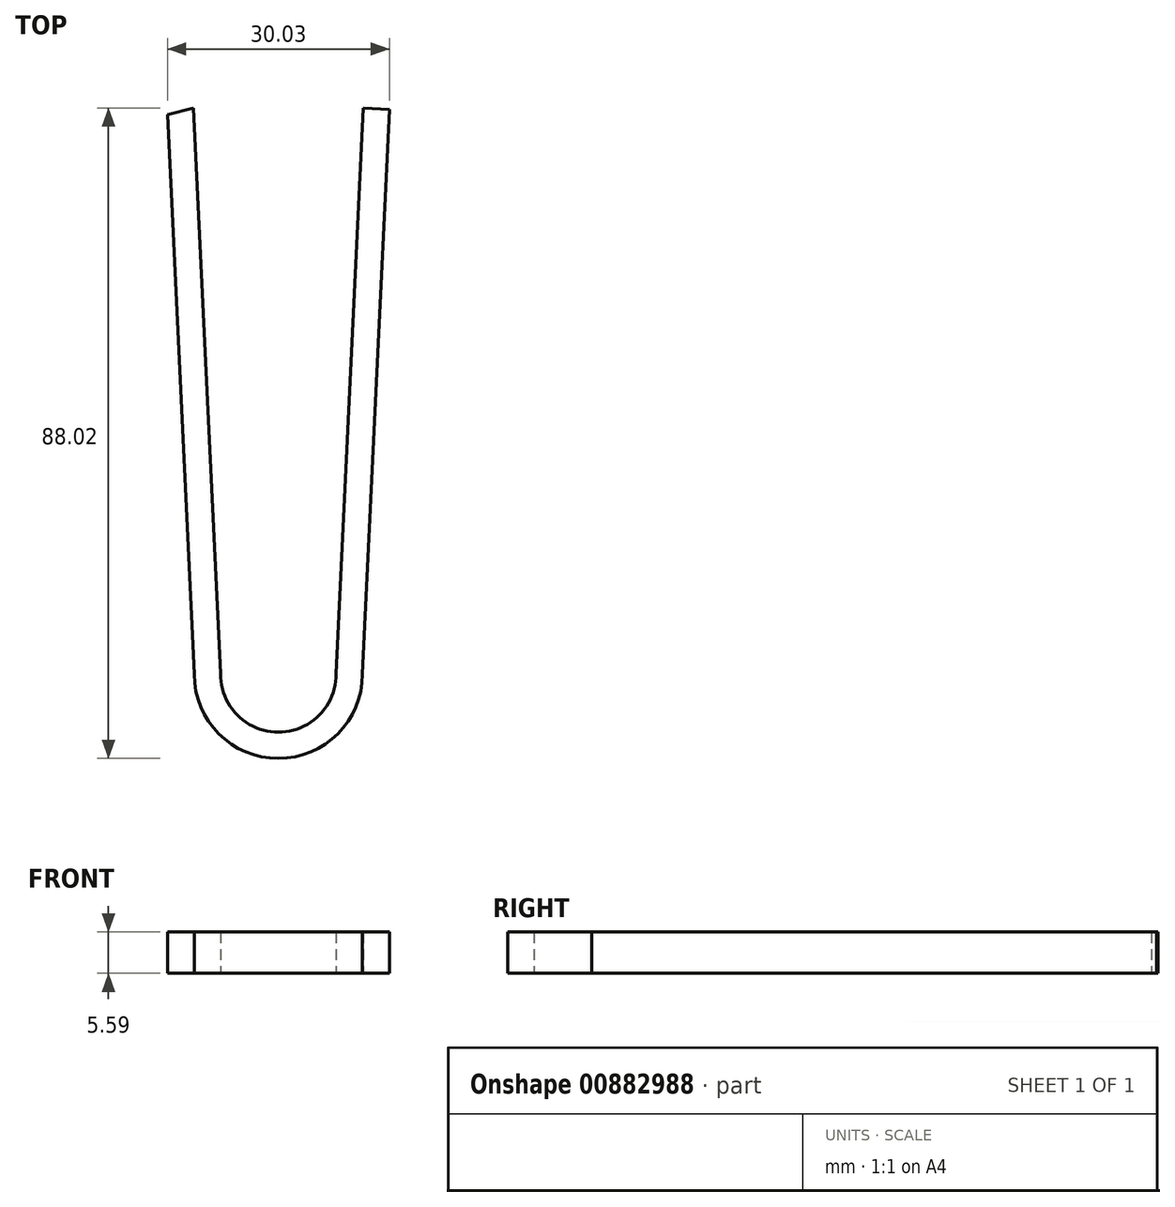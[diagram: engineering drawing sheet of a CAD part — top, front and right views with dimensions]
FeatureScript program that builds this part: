
annotation { "Feature Type Name" : "Feature", "Feature Type Description" : "" }
export const myFeature = defineFeature(function(context is Context, id is Id, definition is map)
    precondition{}
    {
        {
            var Q0;
            Q0=qCreatedBy(makeId("Top.planeOp"),FACE);
            var sketch = newSketch(context, id + "F0", { "sketchPlane" : qUnion([Q0])});
            skArc(sketch, "E0", {"start": v(-11.39, 0) * mm, "mid": v(0, -11.39) * mm, "end": v(11.39, 0) * mm});
            skArc(sketch, "E1", {"start": v(15, 75.74) * mm, "mid": v(15.01, 76.1) * mm, "end": v(15.01, 76.46) * mm});
            skLineSegment(sketch, "E2", {"start": v(-11.39, 0) * mm, "end": v(-15.03, 76.46) * mm});
            skLineSegment(sketch, "E3", {"start": v(11.39, 0) * mm, "end": v(15.03, 76.46) * mm});
            skArc(sketch, "E4.trimOffspring", {"start": v(-15.01, 76.46) * mm, "mid": v(-15.01, 76.1) * mm, "end": v(-15, 75.74) * mm});
            skLineSegment(sketch, "E5.0", {"start": v(-7.83, 0.08) * mm, "end": v(-11.48, 76.63) * mm});
            skArc(sketch, "E5.1", {"start": v(-7.83, 0.08) * mm, "mid": v(0, -7.83) * mm, "end": v(7.83, 0.08) * mm});
            skLineSegment(sketch, "E5.2", {"start": v(7.83, 0.08) * mm, "end": v(11.48, 76.63) * mm});
            skLineSegment(sketch, "E6", {"start": v(-15, 75.74) * mm, "end": v(-11.48, 76.63) * mm});
            skLineSegment(sketch, "E7", {"start": v(15.03, 76.46) * mm, "end": v(11.48, 76.63) * mm});
            skSolve(sketch);
        }
        {
            var Q0;
            Q0 = qSketchRegion(id + "F0", true);
            extrude(context, id + "F1", {"entities" : qUnion([Q0]), "depth" : 5.6 * mm, "offsetDistance" : 25.4 * mm});
        }
    });
